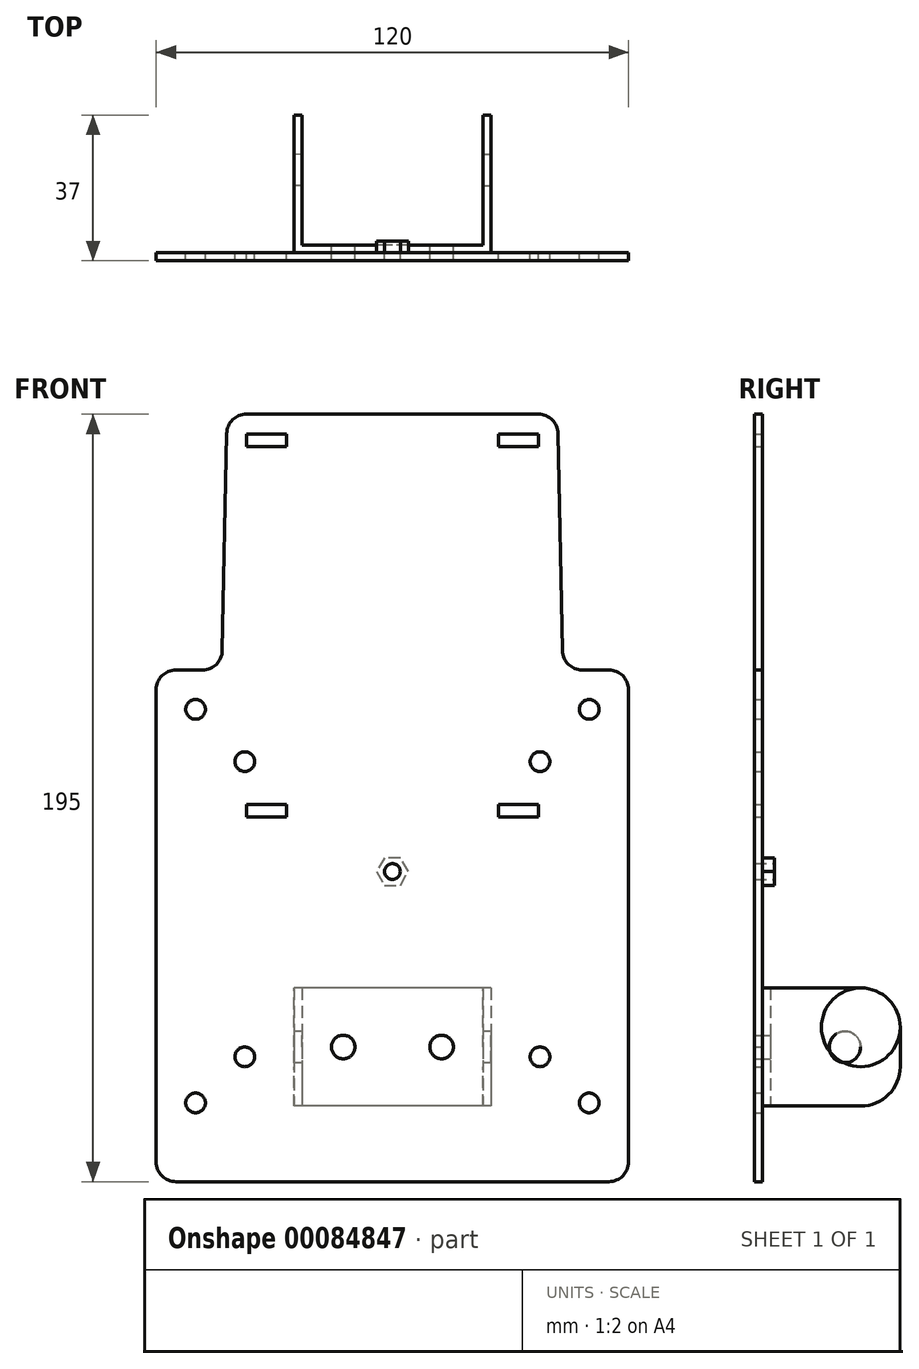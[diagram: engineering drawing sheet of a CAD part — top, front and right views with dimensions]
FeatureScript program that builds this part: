
annotation { "Feature Type Name" : "Feature", "Feature Type Description" : "" }
export const myFeature = defineFeature(function(context is Context, id is Id, definition is map)
    precondition{}
    {
        {
            var Q0;
            Q0=qCreatedBy(makeId("Front.planeOp"),FACE);
            var sketch = newSketch(context, id + "F0", { "sketchPlane" : qUnion([Q0])});
            skCircle(sketch, "E0", {"center": v(-37.5, -37.5) * mm, "radius": 2.5 * mm});
            skCircle(sketch, "E1.0.1.0", {"center": v(-37.5, 37.5) * mm, "radius": 2.5 * mm});
            skLineSegment(sketch, "E1.direction2", {"start": v(-37.5, -37.5) * mm, "end": v(-37.5, 37.5) * mm, "construction": true});
            skCircle(sketch, "E2", {"center": v(-50, -49.22) * mm, "radius": 2.5 * mm});
            skCircle(sketch, "E3.0.1.0", {"center": v(-50, 50.78) * mm, "radius": 2.5 * mm});
            skLineSegment(sketch, "E3.direction2", {"start": v(-50, -49.22) * mm, "end": v(-50, 50.78) * mm, "construction": true});
            skLineSegment(sketch, "E4", {"start": v(0, -69.22) * mm, "end": v(-60, -69.22) * mm});
            skLineSegment(sketch, "E5", {"start": v(-60, -69.22) * mm, "end": v(-60, 60.78) * mm});
            skLineSegment(sketch, "E6", {"start": v(-43.31, 60.78) * mm, "end": v(-42, 125.78) * mm});
            skLineSegment(sketch, "E7", {"start": v(-42, 125.78) * mm, "end": v(0, 125.78) * mm});
            skPoint(sketch, "E8.visualSharp", {"position": v(-60, 60.78) * mm});
            skPoint(sketch, "E9.visualSharp", {"position": v(-42, 125.78) * mm});
            skPoint(sketch, "E10.visualSharp", {"position": v(-43.31, 60.88) * mm});
            skPoint(sketch, "E11.visualSharp", {"position": v(-60, -69.22) * mm});
            skLineSegment(sketch, "E12", {"start": v(0, 125.78) * mm, "end": v(0, 0) * mm, "construction": true});
            skLineSegment(sketch, "E13.bottom", {"start": v(-26.9, 120.78) * mm, "end": v(-37.1, 120.78) * mm});
            skLineSegment(sketch, "E13.top", {"start": v(-26.9, 117.58) * mm, "end": v(-37.1, 117.58) * mm});
            skLineSegment(sketch, "E13.left", {"start": v(-26.9, 120.78) * mm, "end": v(-26.9, 117.58) * mm});
            skLineSegment(sketch, "E13.right", {"start": v(-37.1, 120.78) * mm, "end": v(-37.1, 117.58) * mm});
            skPoint(sketch, "E14", {"position": v(-32, 120.78) * mm});
            skLineSegment(sketch, "E15", {"start": v(0, 0) * mm, "end": v(0, -69.22) * mm, "construction": true});
            skLineSegment(sketch, "E16", {"start": v(-43.31, 60.78) * mm, "end": v(-60, 60.78) * mm});
            skLineSegment(sketch, "E17", {"start": v(-52.13, 72.08) * mm, "end": v(0, 72.08) * mm, "construction": true});
            skLineSegment(sketch, "E18.MirrorCS", {"start": v(-26.9, 23.38) * mm, "end": v(-37.1, 23.38) * mm});
            skLineSegment(sketch, "E19.MirrorCS", {"start": v(-26.9, 23.38) * mm, "end": v(-26.9, 26.58) * mm});
            skLineSegment(sketch, "E20.MirrorCS", {"start": v(-37.1, 23.38) * mm, "end": v(-37.1, 26.58) * mm});
            skLineSegment(sketch, "E21.MirrorCS", {"start": v(-26.9, 26.58) * mm, "end": v(-37.1, 26.58) * mm});
            skPoint(sketch, "E22.MirrorP", {"position": v(-32, 23.38) * mm});
            skLineSegment(sketch, "E23.MirrorCS", {"start": v(37.1, 23.38) * mm, "end": v(37.1, 26.58) * mm});
            skLineSegment(sketch, "E24.MirrorCS", {"start": v(26.9, 117.58) * mm, "end": v(37.1, 117.58) * mm});
            skLineSegment(sketch, "E25.MirrorCS", {"start": v(37.1, 120.78) * mm, "end": v(37.1, 117.58) * mm});
            skLineSegment(sketch, "E26.MirrorCS", {"start": v(26.9, 120.78) * mm, "end": v(26.9, 117.58) * mm});
            skLineSegment(sketch, "E27.MirrorCS", {"start": v(26.9, 120.78) * mm, "end": v(37.1, 120.78) * mm});
            skCircle(sketch, "E28.MirrorC", {"center": v(37.5, 37.5) * mm, "radius": 2.5 * mm});
            skLineSegment(sketch, "E29.MirrorCS", {"start": v(26.9, 23.38) * mm, "end": v(26.9, 26.58) * mm});
            skCircle(sketch, "E30.MirrorC", {"center": v(50, -49.22) * mm, "radius": 2.5 * mm});
            skLineSegment(sketch, "E31.MirrorCS", {"start": v(26.9, 23.38) * mm, "end": v(37.1, 23.38) * mm});
            skCircle(sketch, "E32.MirrorC", {"center": v(37.5, -37.5) * mm, "radius": 2.5 * mm});
            skLineSegment(sketch, "E33.MirrorCS", {"start": v(26.9, 26.58) * mm, "end": v(37.1, 26.58) * mm});
            skCircle(sketch, "E34.MirrorC", {"center": v(50, 50.78) * mm, "radius": 2.5 * mm});
            skLineSegment(sketch, "E35.MirrorCS", {"start": v(43.31, 60.78) * mm, "end": v(60, 60.78) * mm});
            skPoint(sketch, "E36.MirrorP", {"position": v(60, 60.78) * mm});
            skLineSegment(sketch, "E37.MirrorCS", {"start": v(50, -49.22) * mm, "end": v(50, 50.78) * mm, "construction": true});
            skPoint(sketch, "E38.MirrorP", {"position": v(32, 120.78) * mm});
            skLineSegment(sketch, "E39.MirrorCS", {"start": v(0, -69.22) * mm, "end": v(60, -69.22) * mm});
            skLineSegment(sketch, "E40.MirrorCS", {"start": v(43.31, 60.78) * mm, "end": v(42, 125.78) * mm});
            skLineSegment(sketch, "E41.MirrorCS", {"start": v(42, 125.78) * mm, "end": v(0, 125.78) * mm});
            skPoint(sketch, "E42.MirrorP", {"position": v(42, 125.78) * mm});
            skLineSegment(sketch, "E43.MirrorCS", {"start": v(52.13, 72.08) * mm, "end": v(0, 72.08) * mm, "construction": true});
            skLineSegment(sketch, "E44.MirrorCS", {"start": v(37.5, -37.5) * mm, "end": v(37.5, 37.5) * mm, "construction": true});
            skLineSegment(sketch, "E45.MirrorCS", {"start": v(60, -69.22) * mm, "end": v(60, 60.78) * mm});
            skPoint(sketch, "E46.MirrorP", {"position": v(60, -69.22) * mm});
            skPoint(sketch, "E47.MirrorP", {"position": v(32, 23.38) * mm});
            skPoint(sketch, "E48.MirrorP", {"position": v(43.31, 60.88) * mm});
            skCircle(sketch, "E49", {"center": v(0, 9.58) * mm, "radius": 2 * mm});
            skSolve(sketch);
        }
        {
            var Q0;
            Q0=qSketchRegion(id+"F0",true);
            extrude(context, id + "F1", {"entities" : qUnion([Q0]), "depth" : 2 * mm});
        }
        {
            var Q0;
            Q0=makeQuery(id+"F1.opExtrude","SWEPT_EDGE",EDGE,{"disambiguationData":[OSD([sQuery(id+"F0.wireOp",EDGE,"E35.MirrorCS"),sQuery(id+"F0.wireOp",EDGE,"E45.MirrorCS")])]});
            var Q1;
            Q1=makeQuery(id+"F1.opExtrude","SWEPT_EDGE",EDGE,{"disambiguationData":[OSD([sQuery(id+"F0.wireOp",EDGE,"E5"),sQuery(id+"F0.wireOp",EDGE,"E16")])]});
            var Q2;
            Q2=makeQuery(id+"F1.opExtrude","SWEPT_EDGE",EDGE,{"disambiguationData":[OSD([sQuery(id+"F0.wireOp",EDGE,"E6"),sQuery(id+"F0.wireOp",EDGE,"E16")])]});
            var Q3;
            Q3=makeQuery(id+"F1.opExtrude","SWEPT_EDGE",EDGE,{"disambiguationData":[OSD([sQuery(id+"F0.wireOp",EDGE,"E35.MirrorCS"),sQuery(id+"F0.wireOp",EDGE,"E40.MirrorCS")])]});
            var Q4;
            Q4=makeQuery(id+"F1.opExtrude","SWEPT_EDGE",EDGE,{"disambiguationData":[OSD([sQuery(id+"F0.wireOp",EDGE,"E40.MirrorCS"),sQuery(id+"F0.wireOp",EDGE,"E41.MirrorCS")])]});
            var Q5;
            Q5=makeQuery(id+"F1.opExtrude","SWEPT_EDGE",EDGE,{"disambiguationData":[OSD([sQuery(id+"F0.wireOp",EDGE,"E6"),sQuery(id+"F0.wireOp",EDGE,"E7")])]});
            var Q6;
            Q6=makeQuery(id+"F1.opExtrude","SWEPT_EDGE",EDGE,{"disambiguationData":[OSD([sQuery(id+"F0.wireOp",EDGE,"E39.MirrorCS"),sQuery(id+"F0.wireOp",EDGE,"E45.MirrorCS")])]});
            var Q7;
            Q7=makeQuery(id+"F1.opExtrude","SWEPT_EDGE",EDGE,{"disambiguationData":[OSD([sQuery(id+"F0.wireOp",EDGE,"E4"),sQuery(id+"F0.wireOp",EDGE,"E5")])]});
            fillet(context, id + "F2", {"entities" : qUnion([Q0, Q1, Q2, Q3, Q4, Q5, Q6, Q7]), "radius" : 5 * mm, "tangentPropagation" : true, "allowEdgeOverflow" : false});
        }
        {
            var Q0;
            Q0=makeQuery(id+"F1.opExtrude","CAP_FACE",FACE,{"disambiguationData":[OSD([sQuery(id+"F0.wireOp",EDGE,"E0"),sQuery(id+"F0.wireOp",EDGE,"E1.0.1.0"),sQuery(id+"F0.wireOp",EDGE,"E2"),sQuery(id+"F0.wireOp",EDGE,"E3.0.1.0"),sQuery(id+"F0.wireOp",EDGE,"E4"),sQuery(id+"F0.wireOp",EDGE,"E5"),sQuery(id+"F0.wireOp",EDGE,"E6"),sQuery(id+"F0.wireOp",EDGE,"E7"),sQuery(id+"F0.wireOp",EDGE,"E13.bottom"),sQuery(id+"F0.wireOp",EDGE,"E13.top"),sQuery(id+"F0.wireOp",EDGE,"E13.left"),sQuery(id+"F0.wireOp",EDGE,"E13.right"),sQuery(id+"F0.wireOp",EDGE,"E16"),sQuery(id+"F0.wireOp",EDGE,"E18.MirrorCS"),sQuery(id+"F0.wireOp",EDGE,"E19.MirrorCS"),sQuery(id+"F0.wireOp",EDGE,"E20.MirrorCS"),sQuery(id+"F0.wireOp",EDGE,"E21.MirrorCS"),sQuery(id+"F0.wireOp",EDGE,"E23.MirrorCS"),sQuery(id+"F0.wireOp",EDGE,"E24.MirrorCS"),sQuery(id+"F0.wireOp",EDGE,"E25.MirrorCS"),sQuery(id+"F0.wireOp",EDGE,"E26.MirrorCS"),sQuery(id+"F0.wireOp",EDGE,"E27.MirrorCS"),sQuery(id+"F0.wireOp",EDGE,"E28.MirrorC"),sQuery(id+"F0.wireOp",EDGE,"E29.MirrorCS"),sQuery(id+"F0.wireOp",EDGE,"E30.MirrorC"),sQuery(id+"F0.wireOp",EDGE,"E31.MirrorCS"),sQuery(id+"F0.wireOp",EDGE,"E32.MirrorC"),sQuery(id+"F0.wireOp",EDGE,"E33.MirrorCS"),sQuery(id+"F0.wireOp",EDGE,"E34.MirrorC"),sQuery(id+"F0.wireOp",EDGE,"E35.MirrorCS"),sQuery(id+"F0.wireOp",EDGE,"E39.MirrorCS"),sQuery(id+"F0.wireOp",EDGE,"E40.MirrorCS"),sQuery(id+"F0.wireOp",EDGE,"E41.MirrorCS"),sQuery(id+"F0.wireOp",EDGE,"E45.MirrorCS"),sQuery(id+"F0.wireOp",EDGE,"E49")])],"isStart":true});
            var sketch = newSketch(context, id + "F3", { "sketchPlane" : qUnion([Q0])});
            skCircle(sketch, "E50", {"center": v(0, 9.58) * mm, "radius": 2 * mm});
            skCircle(sketch, "E51.cCircle", {"center": v(0, 9.58) * mm, "radius": 3.5 * mm, "construction": true});
            skLineSegment(sketch, "E51.0", {"start": v(2.02, 13.08) * mm, "end": v(4.04, 9.58) * mm});
            skLineSegment(sketch, "E51.1", {"start": v(4.04, 9.58) * mm, "end": v(2.02, 6.08) * mm});
            skLineSegment(sketch, "E51.2", {"start": v(2.02, 6.08) * mm, "end": v(-2.02, 6.08) * mm});
            skLineSegment(sketch, "E51.3", {"start": v(-2.02, 6.08) * mm, "end": v(-4.04, 9.58) * mm});
            skLineSegment(sketch, "E51.4", {"start": v(-4.04, 9.58) * mm, "end": v(-2.02, 13.08) * mm});
            skLineSegment(sketch, "E51.5", {"start": v(-2.02, 13.08) * mm, "end": v(2.02, 13.08) * mm});
            skPoint(sketch, "E51.0.midPoint", {"position": v(3.03, 11.33) * mm});
            skSolve(sketch);
        }
        {
            var Q0;
            Q0=qSketchRegion(id+"F3",true);
            extrude(context, id + "F4", {"entities" : qUnion([Q0]), "operationType" : NewBodyOperationType.ADD, "depth" : 3 * mm});
        }
        {
            var Q0;
            Q0=qCreatedBy(makeId("Top.planeOp"),FACE);
            cPlane(context, id + "F5", {"entities" : qUnion([Q0]), "cplaneType" : CPlaneType.OFFSET, "offset" : 35 * mm, "oppositeDirection" : true, "width" : 150 * mm, "height" : 150 * mm});
        }
        {
            var Q0;
            Q0=qCreatedBy(id+"F5.planeOp",FACE);
            var sketch = newSketch(context, id + "F6", { "sketchPlane" : qUnion([Q0])});
            skLineSegment(sketch, "E52", {"start": v(25, 0) * mm, "end": v(25, 35) * mm});
            skLineSegment(sketch, "E53", {"start": v(25, 35) * mm, "end": v(23, 35) * mm});
            skLineSegment(sketch, "E54", {"start": v(23, 35) * mm, "end": v(23, 2) * mm});
            skLineSegment(sketch, "E55", {"start": v(23, 2) * mm, "end": v(-23, 2) * mm});
            skLineSegment(sketch, "E56", {"start": v(-23, 2) * mm, "end": v(-23, 35) * mm});
            skLineSegment(sketch, "E57", {"start": v(-23, 35) * mm, "end": v(-25, 35) * mm});
            skLineSegment(sketch, "E58", {"start": v(25, 0) * mm, "end": v(-25.02, 0) * mm});
            skLineSegment(sketch, "E59", {"start": v(-25, 35) * mm, "end": v(-25.02, 0) * mm});
            skSolve(sketch);
        }
        {
            var Q0;
            Q0=qSketchRegion(id+"F6",true);
            extrude(context, id + "F7", {"entities" : qUnion([Q0]), "endBound" : BoundingType.SYMMETRIC, "depth" : 30 * mm, "hasSecondDirection" : true, "secondDirectionOppositeDirection" : true, "secondDirectionDepth" : 15 * mm});
        }
        {
            var Q0;
            Q0=makeQuery(id+"F7.opExtrude","CAP_EDGE",EDGE,{"disambiguationData":[OSD([sQuery(id+"F6.wireOp",EDGE,"E53")])],"isStart":false});
            var Q1;
            Q1=makeQuery(id+"F7.opExtrude","CAP_EDGE",EDGE,{"disambiguationData":[OSD([sQuery(id+"F6.wireOp",EDGE,"E53")])],"isStart":true});
            var Q2;
            Q2=makeQuery(id+"F7.opExtrude","CAP_EDGE",EDGE,{"disambiguationData":[OSD([sQuery(id+"F6.wireOp",EDGE,"E57")])],"isStart":true});
            var Q3;
            Q3=makeQuery(id+"F7.opExtrude","CAP_EDGE",EDGE,{"disambiguationData":[OSD([sQuery(id+"F6.wireOp",EDGE,"E57")])],"isStart":false});
            fillet(context, id + "F8", {"entities" : qUnion([Q0, Q1, Q2, Q3]), "radius" : 10 * mm, "tangentPropagation" : true, "allowEdgeOverflow" : false});
        }
        {
            var Q0;
            Q0=makeQuery(id+"F7.opExtrude","SWEPT_FACE",FACE,{"disambiguationData":[OSD([sQuery(id+"F6.wireOp",EDGE,"E59")])]});
            var sketch = newSketch(context, id + "F9", { "sketchPlane" : qUnion([Q0])});
            skCircle(sketch, "E60", {"center": v(-20.99, -35) * mm, "radius": 4 * mm});
            skSolve(sketch);
        }
        {
            var Q0;
            Q0=sQuery(id+"F9.wireOp",VERTEX,"E60.center");
            var Q1;
            Q1=makeQuery(id+"F7.opExtrude","SWEPT_BODY",BODY,{"disambiguationData":[OSD([sQuery(id+"F6.wireOp",EDGE,"xZ2LGaTV-XXyo-5P3s-z8af-GCLrosqeqymj"),sQuery(id+"F6.wireOp",EDGE,"E52"),sQuery(id+"F6.wireOp",EDGE,"E53"),sQuery(id+"F6.wireOp",EDGE,"E54"),sQuery(id+"F6.wireOp",EDGE,"E55"),sQuery(id+"F6.wireOp",EDGE,"E56"),sQuery(id+"F6.wireOp",EDGE,"E57"),sQuery(id+"F6.wireOp",EDGE,"kMLEwMqh-gv4Z-1WQi-TJMr-FqarmwOZAiHq"),sQuery(id+"F6.wireOp",EDGE,"FdXq9dcJ-aUbN-sSeB-byMM-Pfnj8h18ow2l")])]});
            hole(context, id + "F10", {"style" : HoleStyle.SIMPLE, "holeDiameter" : 8 * mm, "endStyle" : HoleEndStyle.BLIND, "holeDepth" : 50 * mm, "locations" : qUnion([Q0]), "scope" : qUnion([Q1])});
        }
        {
            var Q0;
            Q0=makeQuery(id+"F7.opExtrude","SWEPT_FACE",FACE,{"disambiguationData":[OSD([sQuery(id+"F6.wireOp",EDGE,"E55")])]});
            var sketch = newSketch(context, id + "F11", { "sketchPlane" : qUnion([Q0])});
            skCircle(sketch, "E61", {"center": v(-12.5, -35) * mm, "radius": 3 * mm});
            skPoint(sketch, "E61.centerSnap0", {"position": v(-23, -35) * mm});
            skCircle(sketch, "E62.MirrorC", {"center": v(12.5, -35) * mm, "radius": 3 * mm});
            skSolve(sketch);
        }
        {
            var Q0;
            Q0 = qSketchRegion(id + "F11", true);
            extrude(context, id + "F12", {"entities" : qUnion([Q0]), "operationType" : NewBodyOperationType.REMOVE, "oppositeDirection" : true, "depth" : 25 * mm});
        }
    });
